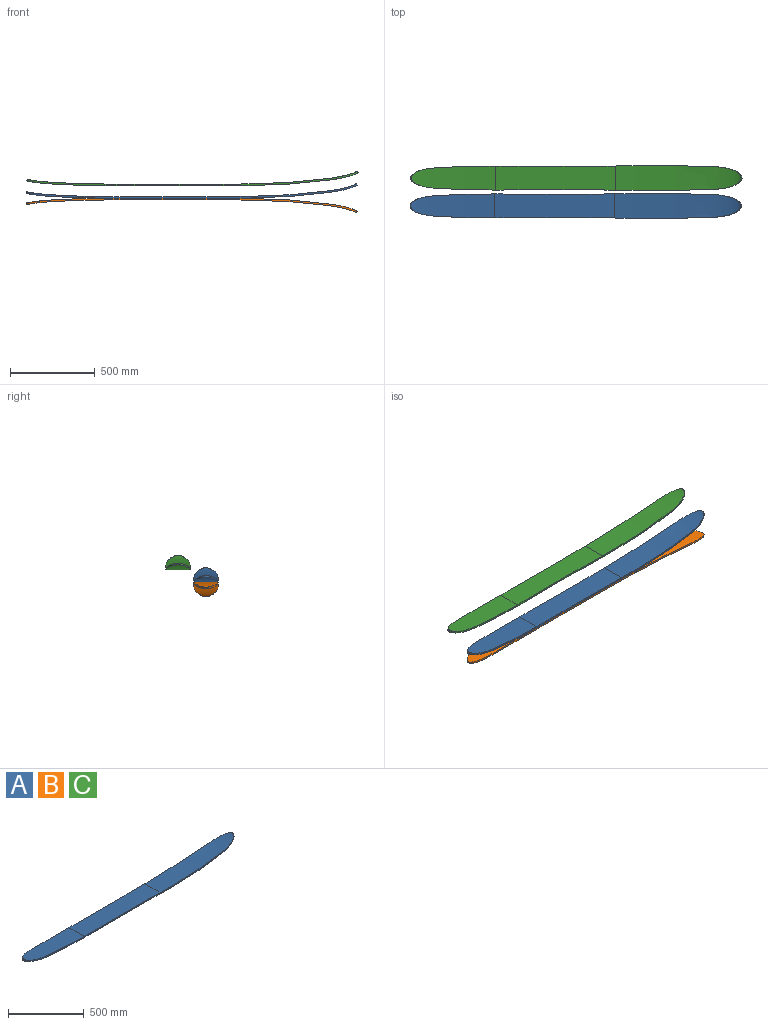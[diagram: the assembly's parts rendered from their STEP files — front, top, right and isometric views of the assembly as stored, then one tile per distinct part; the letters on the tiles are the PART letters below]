
ASSEMBLY  parts=3 mates=1
PART A: 18 faces, bbox 1960x148x86.3 mm
  f0: bspline ~353.52x20.53mm, area 3536.1mm2, adj f1,f11,f12,f15
  f1: extruded ~56.64x10mm, area 566.4mm2, adj f0,f2,f13,f16
  f2: cylinder r=27819.93mm len=653.53mm, axis (0,0,1), area 6535.5mm2, adj f1,f3,f13,f16
  f3: bspline ~111.88x11.02mm, area 1118mm2, adj f2,f4,f14,f17
  f4: bspline ~479.97x43.84mm, area 4807.4mm2, adj f3,f5,f14,f17
  f5: bspline ~160.03x133.46mm, area 3729.6mm2, adj f4,f6,f14,f17
  f6: bspline ~479.97x43.84mm, area 4807.4mm2, adj f5,f7,f14,f17
  f7: bspline ~111.88x11.02mm, area 1118mm2, adj f6,f8,f14,f17
  f8: cylinder r=27819.93mm len=653.53mm, axis (0,0,1), area 6535.5mm2, adj f7,f9,f13,f16
  f9: extruded ~56.64x10mm, area 566.4mm2, adj f8,f10,f13,f16
  f10: bspline ~353.52x20.53mm, area 3536.1mm2, adj f9,f11,f12,f15
  f11: bspline ~146.86x121.2mm, area 3353.6mm2, adj f0,f10,f12,f15
  f12: extruded ~496.49x141.98mm, area 59986.6mm2, adj f0,f10,f11,f13
  f13: plane 710.17x142.44mm, normal (0,0,1), area 99065mm2, adj f1,f2,f8,f9,f12,f14
  f14: extruded ~744.42x145.71mm, area 99775.3mm2, adj f3,f4,f5,f6,f7,f13
  f15: extruded ~499.67x141.98mm, area 60131mm2, adj f0,f10,f11,f16
  f16: plane 710.17x142.44mm, normal (0,0,-1), area 99065mm2, adj f1,f2,f8,f9,f15,f17
  f17: extruded ~750.18x145.71mm, area 100071.3mm2, adj f3,f4,f5,f6,f7,f16
PART B: same geometry as A
PART C: same geometry as A
PLACE A t=(-199.4,-385.39,164.84)mm
PLACE B rot(axis=(1,0,0),180deg) t=(-199.4,-385.39,-15.16)mm
PLACE C t=(-195.68,-220.47,238.45)mm
MATE fastened B.f16 <-> A.f16  axis (0,0,1) through (-804.69,-385.39,74.84)mm
